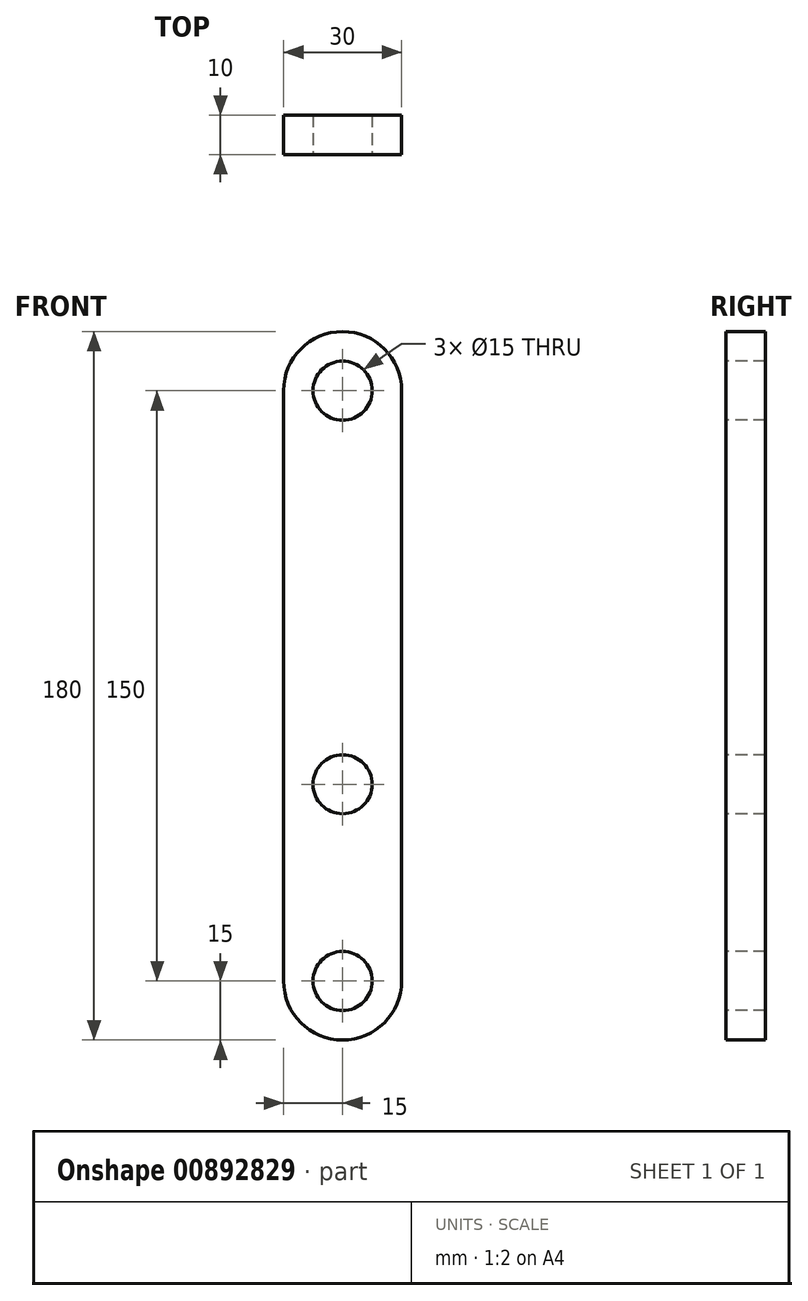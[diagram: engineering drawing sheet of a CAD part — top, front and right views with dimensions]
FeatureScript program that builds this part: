
annotation { "Feature Type Name" : "Feature", "Feature Type Description" : "" }
export const myFeature = defineFeature(function(context is Context, id is Id, definition is map)
    precondition{}
    {
        {
            var Q0;
            Q0=qCreatedBy(makeId("Front.planeOp"),FACE);
            var sketch = newSketch(context, id + "F0", { "sketchPlane" : qUnion([Q0])});
            skArc(sketch, "E0", {"start": v(15, 75) * mm, "mid": v(0, 90) * mm, "end": v(-15, 75) * mm});
            skArc(sketch, "E1", {"start": v(-15, -75) * mm, "mid": v(0, -90) * mm, "end": v(15, -75) * mm});
            skLineSegment(sketch, "E2", {"start": v(-15, 75) * mm, "end": v(-15, -75) * mm});
            skLineSegment(sketch, "E3", {"start": v(15, 75) * mm, "end": v(15, -75) * mm});
            skSolve(sketch);
        }
        {
            var Q0;
            Q0 = qSketchRegion(id + "F0", true);
            var Q1;
            Q1 = qSketchRegion(id + "F6OeOrqVIkfPf0B_0", true);
            extrude(context, id + "F1", {"entities" : qUnion([Q0, Q1]), "depth" : 10 * mm, "offsetDistance" : 25 * mm});
        }
        {
            var Q0;
            Q0=makeQuery(id+"F1.opExtrude","CAP_FACE",FACE,{"disambiguationData":[OSD([sQuery(id+"F0.wireOp",EDGE,"E0"),sQuery(id+"F0.wireOp",EDGE,"E1"),sQuery(id+"F0.wireOp",EDGE,"E2"),sQuery(id+"F0.wireOp",EDGE,"E3")])],"isStart":false});
            var sketch = newSketch(context, id + "F2", { "sketchPlane" : qUnion([Q0])});
            skCircle(sketch, "E4", {"center": v(0, 75) * mm, "radius": 7.5 * mm});
            skCircle(sketch, "E5", {"center": v(0, -75) * mm, "radius": 7.5 * mm});
            skCircle(sketch, "E6", {"center": v(0, -25) * mm, "radius": 7.5 * mm});
            skSolve(sketch);
        }
        {
            var Q0;
            Q0 = qSketchRegion(id + "F2", true);
            extrude(context, id + "F3", {"entities" : qUnion([Q0]), "operationType" : NewBodyOperationType.REMOVE, "endBound" : BoundingType.SYMMETRIC, "oppositeDirection" : true, "depth" : 50 * mm, "offsetDistance" : 25 * mm});
        }
    });
